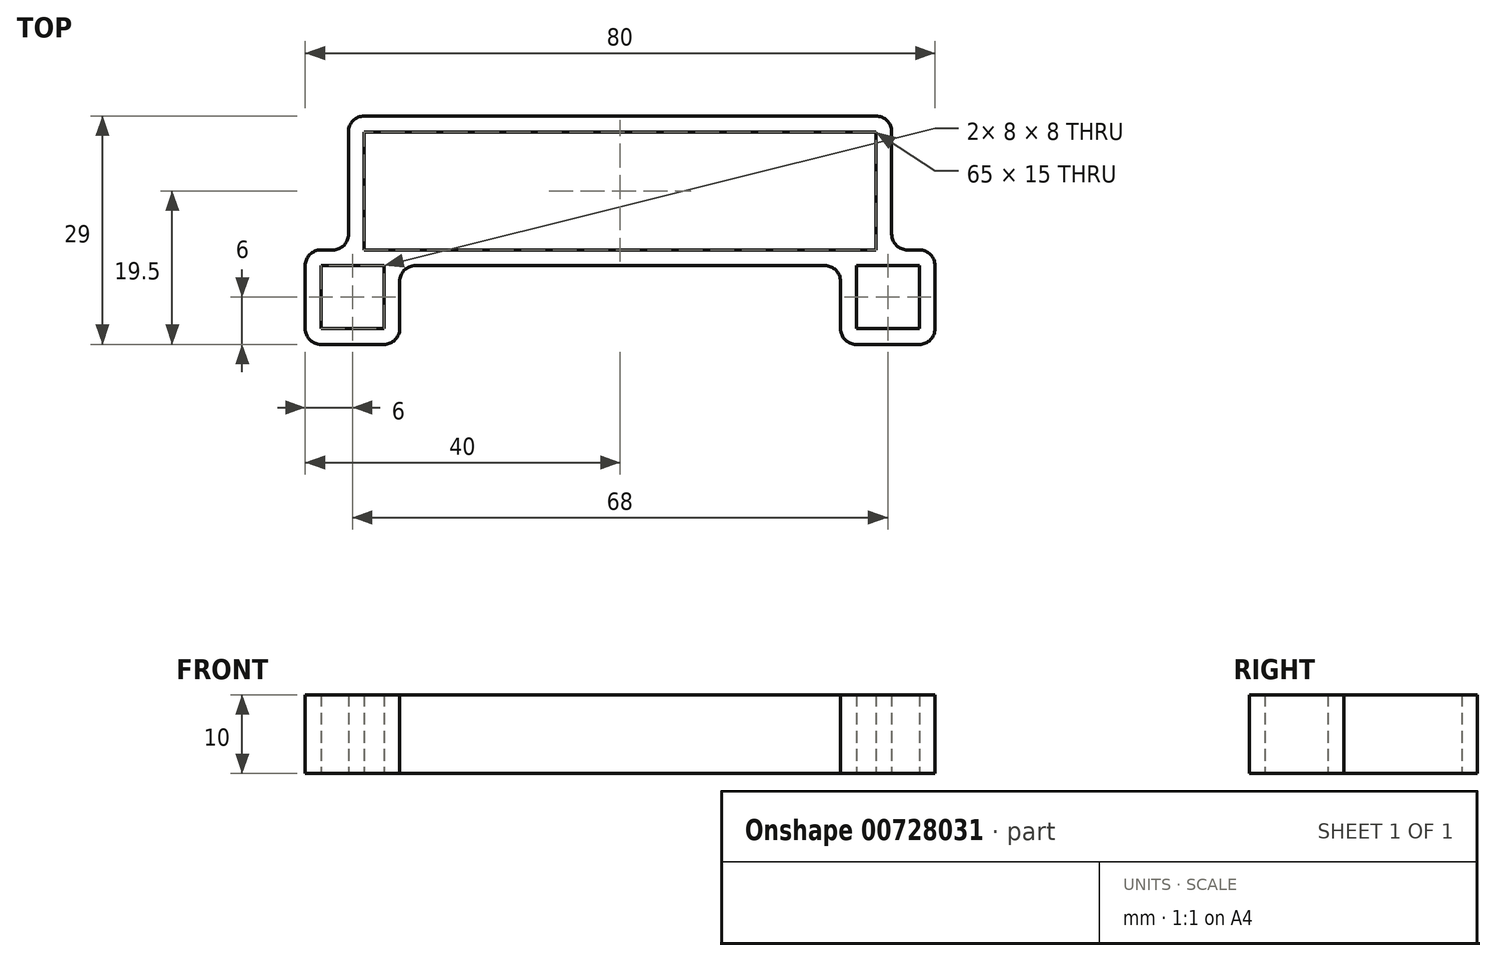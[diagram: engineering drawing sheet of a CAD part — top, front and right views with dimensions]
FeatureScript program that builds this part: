
annotation { "Feature Type Name" : "Feature", "Feature Type Description" : "" }
export const myFeature = defineFeature(function(context is Context, id is Id, definition is map)
    precondition{}
    {
        {
            var Q0;
            Q0=qCreatedBy(makeId("Top.planeOp"),FACE);
            var sketch = newSketch(context, id + "F0", { "sketchPlane" : qUnion([Q0])});
            skLineSegment(sketch, "E0.top", {"start": v(-28, -6) * mm, "end": v(-40, -6) * mm});
            skLineSegment(sketch, "E0.left", {"start": v(-28, 4) * mm, "end": v(-28, -6) * mm});
            skLineSegment(sketch, "E0.right", {"start": v(-40, 6) * mm, "end": v(-40, -6) * mm});
            skPoint(sketch, "E0.middle", {"position": v(-34, 0) * mm});
            skLineSegment(sketch, "E1.bottom", {"start": v(-34.5, 4) * mm, "end": v(-38, 4) * mm});
            skLineSegment(sketch, "E1.top", {"start": v(-30, -4) * mm, "end": v(-38, -4) * mm});
            skLineSegment(sketch, "E1.left", {"start": v(-30, 4) * mm, "end": v(-30, -4) * mm});
            skLineSegment(sketch, "E1.right", {"start": v(-38, 4) * mm, "end": v(-38, -4) * mm});
            skPoint(sketch, "E2.MirrorP", {"position": v(34, 0) * mm});
            skLineSegment(sketch, "E3.MirrorCS", {"start": v(30, -4) * mm, "end": v(38, -4) * mm});
            skLineSegment(sketch, "E4.MirrorCS", {"start": v(28, -6) * mm, "end": v(40, -6) * mm});
            skLineSegment(sketch, "E5.MirrorCS", {"start": v(34.5, 4) * mm, "end": v(38, 4) * mm});
            skLineSegment(sketch, "E6.MirrorCS", {"start": v(38, 4) * mm, "end": v(38, -4) * mm});
            skLineSegment(sketch, "E7.MirrorCS", {"start": v(28, 4) * mm, "end": v(28, -6) * mm});
            skLineSegment(sketch, "E8.MirrorCS", {"start": v(40, 6) * mm, "end": v(40, -6) * mm});
            skLineSegment(sketch, "E9.MirrorCS", {"start": v(30, 4) * mm, "end": v(30, -4) * mm});
            skPoint(sketch, "E10.middle", {"position": v(0, 13.5) * mm});
            skLineSegment(sketch, "E11.bottom", {"start": v(34.5, 23) * mm, "end": v(-34.5, 23) * mm});
            skLineSegment(sketch, "E11.top", {"start": v(34.5, 4) * mm, "end": v(30, 4) * mm});
            skLineSegment(sketch, "E11.left", {"start": v(34.5, 23) * mm, "end": v(34.5, 6) * mm});
            skLineSegment(sketch, "E11.right", {"start": v(-34.5, 23) * mm, "end": v(-34.5, 6) * mm});
            skLineSegment(sketch, "E12.trimOffspring", {"start": v(-34.5, 6) * mm, "end": v(-40, 6) * mm});
            skLineSegment(sketch, "E13.trimOffspring", {"start": v(-30, 4) * mm, "end": v(-34.5, 4) * mm});
            skLineSegment(sketch, "E14.trimOffspring", {"start": v(28, 4) * mm, "end": v(-28, 4) * mm});
            skLineSegment(sketch, "E15.trimOffspring", {"start": v(34.5, 6) * mm, "end": v(40, 6) * mm});
            skLineSegment(sketch, "E16.bottom", {"start": v(32.5, 21) * mm, "end": v(-32.5, 21) * mm});
            skLineSegment(sketch, "E16.top", {"start": v(32.5, 6) * mm, "end": v(-32.5, 6) * mm});
            skLineSegment(sketch, "E16.left", {"start": v(32.5, 21) * mm, "end": v(32.5, 6) * mm});
            skLineSegment(sketch, "E16.right", {"start": v(-32.5, 21) * mm, "end": v(-32.5, 6) * mm});
            skSolve(sketch);
        }
        {
            var Q0;
            Q0=makeQuery(id+"F0.imprint","IMPRINT",FACE,{"disambiguationData":[TD([[makeQuery(id+"F0.imprint","IMPRINT",EDGE,{"derivedFrom":sQuery(id+"F0.wireOp",EDGE,"E0.top")}),-1.0]])]});
            extrude(context, id + "F1", {"entities" : qUnion([Q0]), "depth" : 10 * mm, "offsetDistance" : 25 * mm});
        }
        {
            var Q0;
            Q0=makeQuery(id+"F1.opExtrude","SWEPT_EDGE",EDGE,{"disambiguationData":[OSD([sQuery(id+"F0.wireOp",EDGE,"E11.bottom"),sQuery(id+"F0.wireOp",EDGE,"E11.right")])]});
            var Q1;
            Q1=makeQuery(id+"F1.opExtrude","SWEPT_EDGE",EDGE,{"disambiguationData":[OSD([sQuery(id+"F0.wireOp",EDGE,"E0.right"),sQuery(id+"F0.wireOp",EDGE,"E12.trimOffspring")])]});
            var Q2;
            Q2=makeQuery(id+"F1.opExtrude","SWEPT_EDGE",EDGE,{"disambiguationData":[OSD([sQuery(id+"F0.wireOp",EDGE,"E0.top"),sQuery(id+"F0.wireOp",EDGE,"E0.right")])]});
            var Q3;
            Q3=makeQuery(id+"F1.opExtrude","SWEPT_EDGE",EDGE,{"disambiguationData":[OSD([sQuery(id+"F0.wireOp",EDGE,"E0.top"),sQuery(id+"F0.wireOp",EDGE,"E0.left")])]});
            var Q4;
            Q4=makeQuery(id+"F1.opExtrude","SWEPT_EDGE",EDGE,{"disambiguationData":[OSD([sQuery(id+"F0.wireOp",EDGE,"E0.left"),sQuery(id+"F0.wireOp",EDGE,"E14.trimOffspring")])]});
            var Q5;
            Q5=makeQuery(id+"F1.opExtrude","SWEPT_EDGE",EDGE,{"disambiguationData":[OSD([sQuery(id+"F0.wireOp",EDGE,"E11.right"),sQuery(id+"F0.wireOp",EDGE,"E12.trimOffspring")])]});
            var Q6;
            Q6=makeQuery(id+"F1.opExtrude","SWEPT_EDGE",EDGE,{"disambiguationData":[OSD([sQuery(id+"F0.wireOp",EDGE,"E11.bottom"),sQuery(id+"F0.wireOp",EDGE,"E11.left")])]});
            var Q7;
            Q7=makeQuery(id+"F1.opExtrude","SWEPT_EDGE",EDGE,{"disambiguationData":[OSD([sQuery(id+"F0.wireOp",EDGE,"E11.left"),sQuery(id+"F0.wireOp",EDGE,"E15.trimOffspring")])]});
            var Q8;
            Q8=makeQuery(id+"F1.opExtrude","SWEPT_EDGE",EDGE,{"disambiguationData":[OSD([sQuery(id+"F0.wireOp",EDGE,"E8.MirrorCS"),sQuery(id+"F0.wireOp",EDGE,"E15.trimOffspring")])]});
            var Q9;
            Q9=makeQuery(id+"F1.opExtrude","SWEPT_EDGE",EDGE,{"disambiguationData":[OSD([sQuery(id+"F0.wireOp",EDGE,"E4.MirrorCS"),sQuery(id+"F0.wireOp",EDGE,"E8.MirrorCS")])]});
            var Q10;
            Q10=makeQuery(id+"F1.opExtrude","SWEPT_EDGE",EDGE,{"disambiguationData":[OSD([sQuery(id+"F0.wireOp",EDGE,"E7.MirrorCS"),sQuery(id+"F0.wireOp",EDGE,"E14.trimOffspring")])]});
            var Q11;
            Q11=makeQuery(id+"F1.opExtrude","SWEPT_EDGE",EDGE,{"disambiguationData":[OSD([sQuery(id+"F0.wireOp",EDGE,"E4.MirrorCS"),sQuery(id+"F0.wireOp",EDGE,"E7.MirrorCS")])]});
            fillet(context, id + "F2", {"entities" : qUnion([Q0, Q1, Q2, Q3, Q4, Q5, Q6, Q7, Q8, Q9, Q10, Q11]), "radius" : 2 * mm, "tangentPropagation" : true, "allowEdgeOverflow" : false});
        }
    });
